# Revit family: Tub_Spout-American_Standard-Berwick-8888.743.002
name_source: partatom
category: Plumbing Fixtures
revit_build: Autodesk Revit 2015 (Build: 20140606_1530(x64)
units: mm (PartAtom-declared; Revit-internal decimal feet)

## types (3) — shared parameters
ADA Compliant = Yes
Assembly Code = D2020300
CW Connection = Yes
CWFU = 2
Cold Water Connection Diameter = 1/2"
Cold Water Connection Height = 39"
Cold Water Connection Radius = 1/4"
Default Elevation = 0"
Finish = Brass-American Standard-002-Polished Chrome
HW Connection = Yes
HWFU = 3
Height = 74"
Hot Water Connection Diameter = 1/2"
Hot Water Connection Height = 39"
Hot Water Connection Radius = 1/4"
Length = 12"
Manufacturer = American Standard
Material = Brass-American Standard-002-Polished Chrome
NPT Connection Radius = 1/4"
NPT Connection Size = 1/2"
Price = Prices may vary. Please consult Manufacturer Representative for most up-to-date price list.
Product Documentation Link = https://www.americanstandard-us.com
Product Page URL = https://www.americanstandard-us.com
Revised Date = 11/18/2016
URL = http://www.americanstandard-us.com
Valve = Yes
Vent Connection = No
WFU = 4
Warranty Information = Limited Lifetime Function and Finish Warranty.
Waste Connection = No
Width = 7 1/4"

## per-type parameters (varying)
| type | Bath | Description | Shower |
| T430.502 | Yes | Berwick Pressure Balance Bath/Shower Fitting. Bath and Shower Trim kit. | Yes |
| T430.501 | No | Berwick Pressure Balance Bath/Shower Fitting. Shower Only. | Yes |
| T430.500 | No | Berwick Pressure Balance Bath/Shower Fitting. Shower Only. Valve Only. | No |

note: column(s) folded — value = type name in every type: Model

## geometry (parser evidence)
native form markers: Sweep x3
no freeform markers — native parametric forms only
